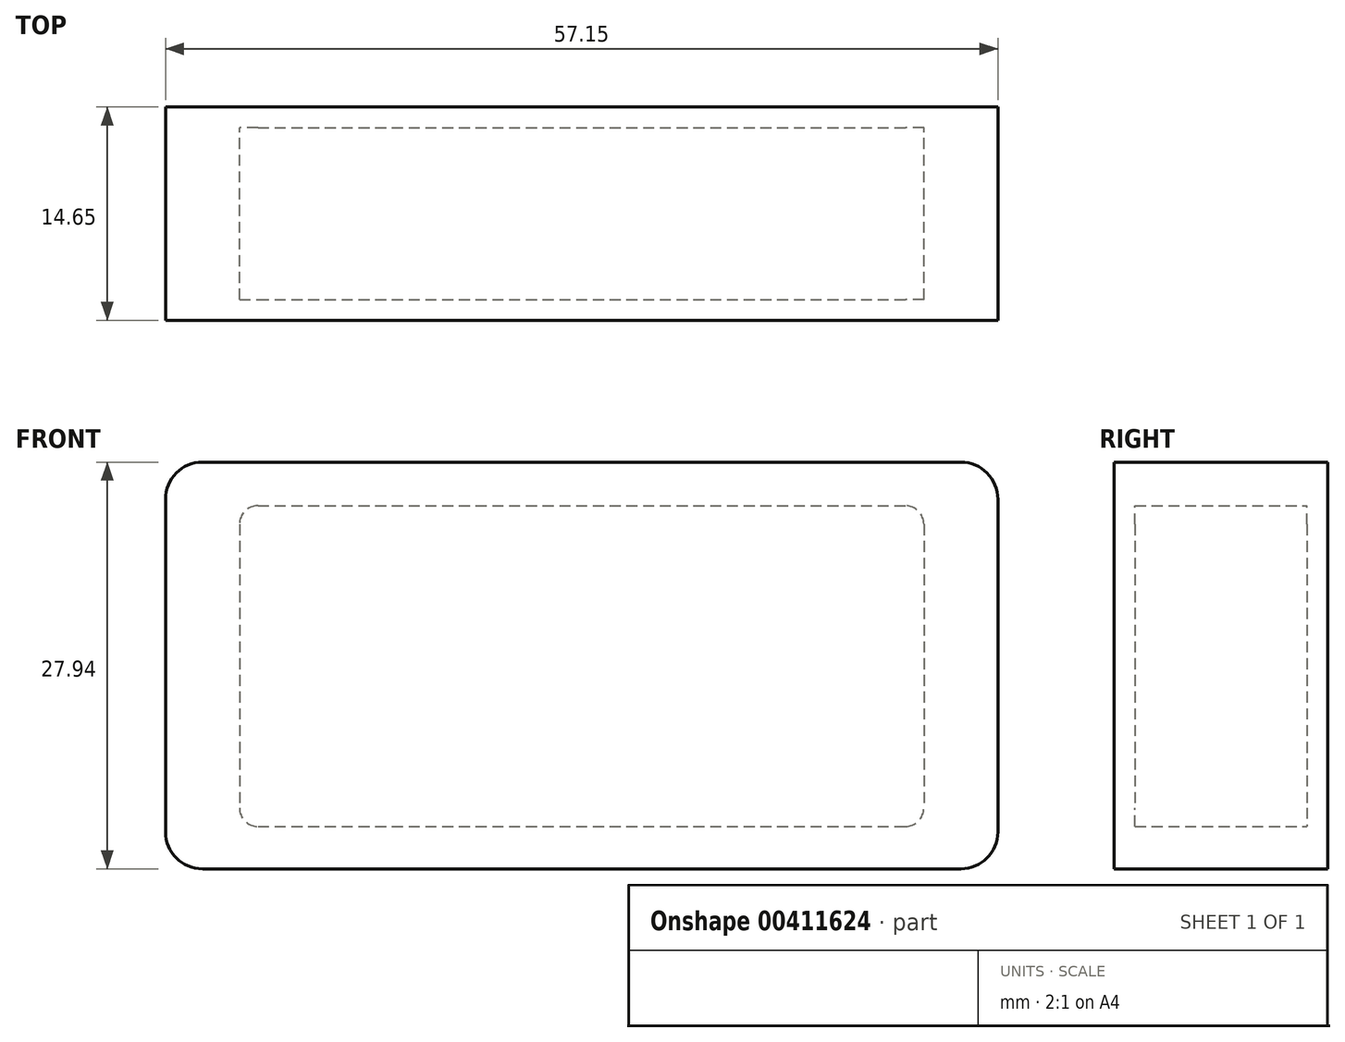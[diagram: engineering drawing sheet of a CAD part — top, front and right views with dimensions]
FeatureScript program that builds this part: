
annotation { "Feature Type Name" : "Feature", "Feature Type Description" : "" }
export const myFeature = defineFeature(function(context is Context, id is Id, definition is map)
    precondition{}
    {
        {
            var Q0;
            Q0=qCreatedBy(makeId("Front.planeOp"),FACE);
            var sketch = newSketch(context, id + "F0", { "sketchPlane" : qUnion([Q0])});
            skLineSegment(sketch, "E0.bottom", {"start": v(2.54, 0) * mm, "end": v(54.6, 0) * mm});
            skLineSegment(sketch, "E0.top", {"start": v(2.54, -27.94) * mm, "end": v(54.6, -27.94) * mm});
            skLineSegment(sketch, "E0.left", {"start": v(0, -2.54) * mm, "end": v(0, -25.4) * mm});
            skLineSegment(sketch, "E0.right", {"start": v(57.15, -2.54) * mm, "end": v(57.15, -25.4) * mm});
            skLineSegment(sketch, "E1.bottom", {"start": v(6.35, -3) * mm, "end": v(50.8, -3) * mm});
            skLineSegment(sketch, "E1.top", {"start": v(6.35, -25.02) * mm, "end": v(50.8, -25.02) * mm});
            skLineSegment(sketch, "E1.left", {"start": v(5.08, -4.27) * mm, "end": v(5.08, -23.75) * mm});
            skLineSegment(sketch, "E1.right", {"start": v(52.07, -4.27) * mm, "end": v(52.07, -23.75) * mm});
            skPoint(sketch, "E2.visualSharp", {"position": v(5.08, -3) * mm});
            skArc(sketch, "E2.filletArc", {"start": v(6.35, -3) * mm, "mid": v(5.45, -3.37) * mm, "end": v(5.08, -4.27) * mm});
            skPoint(sketch, "E3.visualSharp", {"position": v(52.07, -3) * mm});
            skArc(sketch, "E3.filletArc", {"start": v(52.07, -4.27) * mm, "mid": v(51.7, -3.37) * mm, "end": v(50.8, -3) * mm});
            skPoint(sketch, "E4.visualSharp", {"position": v(52.07, -25.02) * mm});
            skArc(sketch, "E4.filletArc", {"start": v(50.8, -25.02) * mm, "mid": v(51.7, -24.65) * mm, "end": v(52.07, -23.75) * mm});
            skPoint(sketch, "E5.visualSharp", {"position": v(5.08, -25.02) * mm});
            skArc(sketch, "E5.filletArc", {"start": v(5.08, -23.75) * mm, "mid": v(5.45, -24.65) * mm, "end": v(6.35, -25.02) * mm});
            skPoint(sketch, "E6.visualSharp", {"position": v(0, 0) * mm});
            skArc(sketch, "E6.filletArc", {"start": v(2.54, 0) * mm, "mid": v(0.74, -0.74) * mm, "end": v(0, -2.54) * mm});
            skPoint(sketch, "E7.visualSharp", {"position": v(0, -27.94) * mm});
            skArc(sketch, "E7.filletArc", {"start": v(0, -25.4) * mm, "mid": v(0.74, -27.2) * mm, "end": v(2.54, -27.94) * mm});
            skPoint(sketch, "E8.visualSharp", {"position": v(57.15, -27.94) * mm});
            skArc(sketch, "E8.filletArc", {"start": v(54.6, -27.94) * mm, "mid": v(56.4, -27.2) * mm, "end": v(57.15, -25.4) * mm});
            skPoint(sketch, "E9.visualSharp", {"position": v(57.15, 0) * mm});
            skArc(sketch, "E9.filletArc", {"start": v(57.15, -2.54) * mm, "mid": v(56.4, -0.74) * mm, "end": v(54.6, 0) * mm});
            skSolve(sketch);
        }
        {
            var Q0;
            Q0=makeQuery(id+"F0.imprint","IMPRINT",FACE,{"disambiguationData":[TD([[makeQuery(id+"F0.imprint","IMPRINT",EDGE,{"derivedFrom":sQuery(id+"F0.wireOp",EDGE,"E0.bottom")}),-1.0]])]});
            extrude(context, id + "F1", {"entities" : qUnion([Q0]), "depth" : 11.8 * mm});
        }
        {
            var Q0;
            Q0=makeQuery(id+"F1.opExtrude","CAP_FACE",FACE,{"disambiguationData":[OSD([sQuery(id+"F0.wireOp",EDGE,"E0.bottom"),sQuery(id+"F0.wireOp",EDGE,"E0.top"),sQuery(id+"F0.wireOp",EDGE,"E0.left"),sQuery(id+"F0.wireOp",EDGE,"E0.right"),sQuery(id+"F0.wireOp",EDGE,"E1.bottom"),sQuery(id+"F0.wireOp",EDGE,"E1.top"),sQuery(id+"F0.wireOp",EDGE,"E1.left"),sQuery(id+"F0.wireOp",EDGE,"E1.right"),sQuery(id+"F0.wireOp",EDGE,"E2.filletArc"),sQuery(id+"F0.wireOp",EDGE,"E3.filletArc"),sQuery(id+"F0.wireOp",EDGE,"E4.filletArc"),sQuery(id+"F0.wireOp",EDGE,"E5.filletArc"),sQuery(id+"F0.wireOp",EDGE,"E6.filletArc"),sQuery(id+"F0.wireOp",EDGE,"E7.filletArc"),sQuery(id+"F0.wireOp",EDGE,"E8.filletArc"),sQuery(id+"F0.wireOp",EDGE,"E9.filletArc")])],"isStart":true});
            var sketch = newSketch(context, id + "F2", { "sketchPlane" : qUnion([Q0])});
            skLineSegment(sketch, "E10.bottom", {"start": v(-2.54, 0) * mm, "end": v(-54.6, 0) * mm});
            skLineSegment(sketch, "E10.top", {"start": v(-2.54, -27.94) * mm, "end": v(-54.6, -27.94) * mm});
            skLineSegment(sketch, "E10.left", {"start": v(0, -2.54) * mm, "end": v(0, -25.4) * mm});
            skLineSegment(sketch, "E10.right", {"start": v(-57.15, -2.54) * mm, "end": v(-57.15, -25.4) * mm});
            skPoint(sketch, "E11.visualSharp", {"position": v(0, 0) * mm});
            skArc(sketch, "E11.filletArc", {"start": v(0, -2.54) * mm, "mid": v(-0.74, -0.74) * mm, "end": v(-2.54, 0) * mm});
            skPoint(sketch, "E12.visualSharp", {"position": v(-57.15, 0) * mm});
            skArc(sketch, "E12.filletArc", {"start": v(-54.6, 0) * mm, "mid": v(-56.4, -0.74) * mm, "end": v(-57.15, -2.54) * mm});
            skPoint(sketch, "E13.visualSharp", {"position": v(-57.15, -27.94) * mm});
            skArc(sketch, "E13.filletArc", {"start": v(-57.15, -25.4) * mm, "mid": v(-56.4, -27.2) * mm, "end": v(-54.6, -27.94) * mm});
            skPoint(sketch, "E14.visualSharp", {"position": v(0, -27.94) * mm});
            skArc(sketch, "E14.filletArc", {"start": v(-2.54, -27.94) * mm, "mid": v(-0.74, -27.2) * mm, "end": v(0, -25.4) * mm});
            skSolve(sketch);
        }
        {
            var Q0;
            Q0 = qSketchRegion(id + "F2", true);
            extrude(context, id + "F3", {"entities" : qUnion([Q0]), "operationType" : NewBodyOperationType.ADD, "depth" : 1.42 * mm});
        }
        {
            var Q0;
            Q0=makeQuery(id+"F1.opExtrude","CAP_FACE",FACE,{"disambiguationData":[OSD([sQuery(id+"F0.wireOp",EDGE,"E0.bottom"),sQuery(id+"F0.wireOp",EDGE,"E0.top"),sQuery(id+"F0.wireOp",EDGE,"E0.left"),sQuery(id+"F0.wireOp",EDGE,"E0.right"),sQuery(id+"F0.wireOp",EDGE,"E1.bottom"),sQuery(id+"F0.wireOp",EDGE,"E1.top"),sQuery(id+"F0.wireOp",EDGE,"E1.left"),sQuery(id+"F0.wireOp",EDGE,"E1.right"),sQuery(id+"F0.wireOp",EDGE,"E2.filletArc"),sQuery(id+"F0.wireOp",EDGE,"E3.filletArc"),sQuery(id+"F0.wireOp",EDGE,"E4.filletArc"),sQuery(id+"F0.wireOp",EDGE,"E5.filletArc"),sQuery(id+"F0.wireOp",EDGE,"E6.filletArc"),sQuery(id+"F0.wireOp",EDGE,"E7.filletArc"),sQuery(id+"F0.wireOp",EDGE,"E8.filletArc"),sQuery(id+"F0.wireOp",EDGE,"E9.filletArc")])],"isStart":false});
            var sketch = newSketch(context, id + "F4", { "sketchPlane" : qUnion([Q0])});
            skLineSegment(sketch, "E15.bottom", {"start": v(2.54, 0) * mm, "end": v(54.6, 0) * mm});
            skLineSegment(sketch, "E15.top", {"start": v(2.54, -27.94) * mm, "end": v(54.6, -27.94) * mm});
            skLineSegment(sketch, "E15.left", {"start": v(0, -2.54) * mm, "end": v(0, -25.4) * mm});
            skLineSegment(sketch, "E15.right", {"start": v(57.15, -2.54) * mm, "end": v(57.15, -25.4) * mm});
            skPoint(sketch, "E16.visualSharp", {"position": v(0, 0) * mm});
            skArc(sketch, "E16.filletArc", {"start": v(2.54, 0) * mm, "mid": v(0.74, -0.74) * mm, "end": v(0, -2.54) * mm});
            skPoint(sketch, "E17.visualSharp", {"position": v(57.15, 0) * mm});
            skArc(sketch, "E17.filletArc", {"start": v(57.15, -2.54) * mm, "mid": v(56.4, -0.74) * mm, "end": v(54.6, 0) * mm});
            skPoint(sketch, "E18.visualSharp", {"position": v(57.15, -27.94) * mm});
            skArc(sketch, "E18.filletArc", {"start": v(54.6, -27.94) * mm, "mid": v(56.4, -27.2) * mm, "end": v(57.15, -25.4) * mm});
            skPoint(sketch, "E19.visualSharp", {"position": v(0, -27.94) * mm});
            skArc(sketch, "E19.filletArc", {"start": v(0, -25.4) * mm, "mid": v(0.74, -27.2) * mm, "end": v(2.54, -27.94) * mm});
            skSolve(sketch);
        }
        {
            var Q0;
            Q0 = qSketchRegion(id + "F4", true);
            extrude(context, id + "F5", {"entities" : qUnion([Q0]), "operationType" : NewBodyOperationType.ADD, "depth" : 1.42 * mm});
        }
    });
